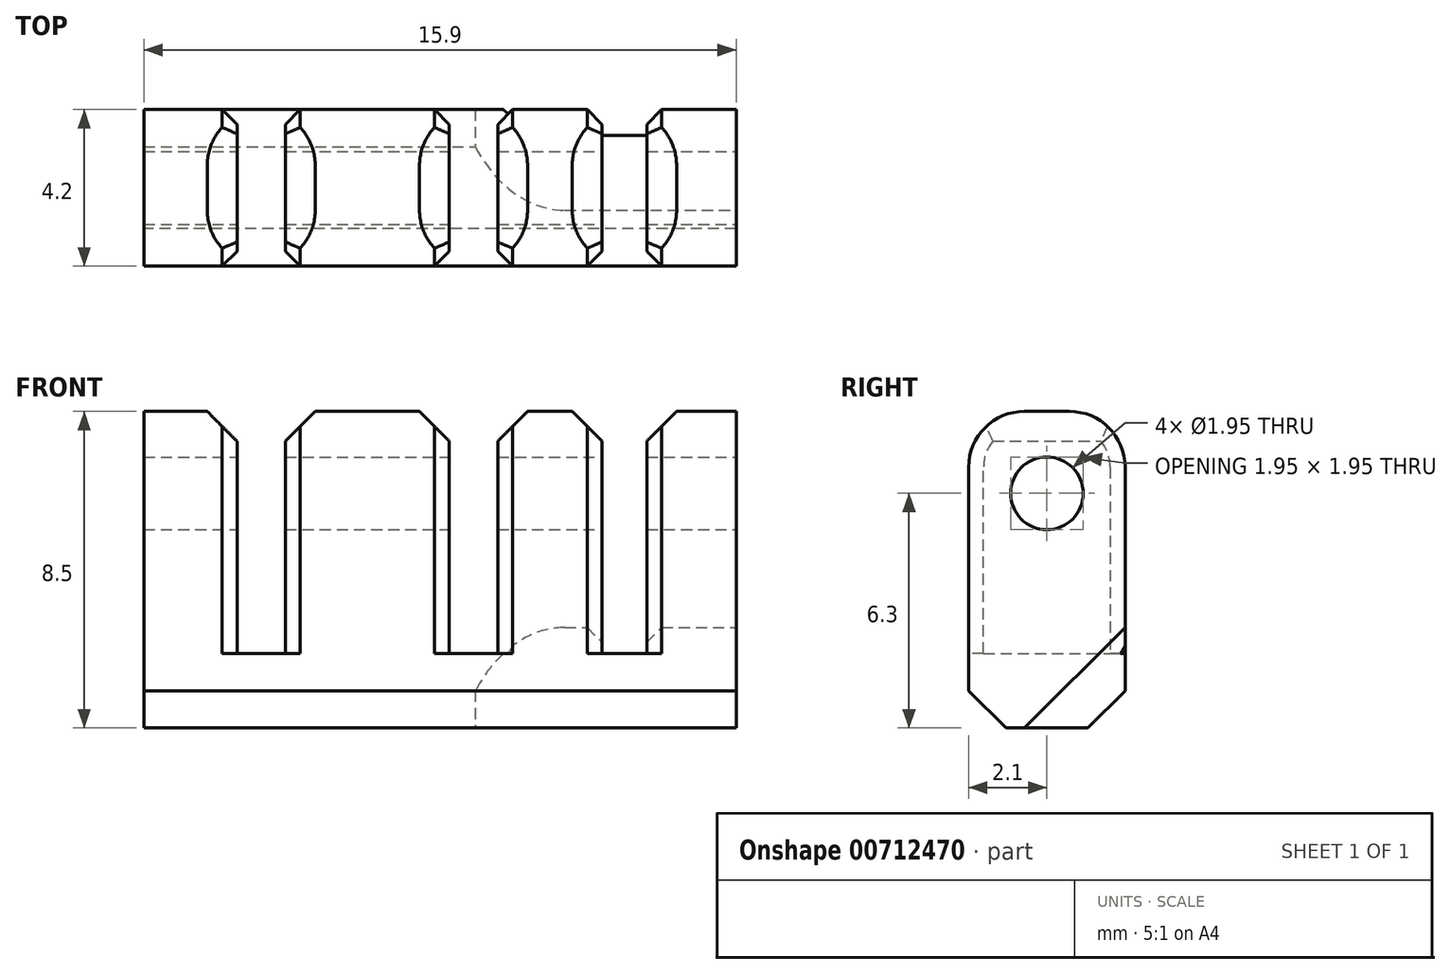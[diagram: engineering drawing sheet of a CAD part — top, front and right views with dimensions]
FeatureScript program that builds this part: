
annotation { "Feature Type Name" : "Feature", "Feature Type Description" : "" }
export const myFeature = defineFeature(function(context is Context, id is Id, definition is map)
    precondition{}
    {
        {
            var Q0;
            Q0=qCreatedBy(makeId("Front.planeOp"),FACE);
            var sketch = newSketch(context, id + "F0", { "sketchPlane" : qUnion([Q0])});
            skLineSegment(sketch, "E0", {"start": v(0, 0) * mm, "end": v(15.9, 0) * mm});
            skLineSegment(sketch, "E1", {"start": v(15.9, 0) * mm, "end": v(15.9, 8.5) * mm});
            skLineSegment(sketch, "E2", {"start": v(15.9, 8.5) * mm, "end": v(13.5, 8.5) * mm});
            skLineSegment(sketch, "E3", {"start": v(13.5, 8.5) * mm, "end": v(13.5, 2) * mm});
            skLineSegment(sketch, "E4", {"start": v(13.5, 2) * mm, "end": v(12.3, 2) * mm});
            skLineSegment(sketch, "E5", {"start": v(12.3, 2) * mm, "end": v(12.3, 8.5) * mm});
            skLineSegment(sketch, "E6", {"start": v(12.3, 8.5) * mm, "end": v(9.5, 8.5) * mm});
            skLineSegment(sketch, "E7", {"start": v(9.5, 8.5) * mm, "end": v(9.5, 2) * mm});
            skLineSegment(sketch, "E8", {"start": v(9.5, 2) * mm, "end": v(8.2, 2) * mm});
            skLineSegment(sketch, "E9", {"start": v(8.2, 2) * mm, "end": v(8.2, 8.5) * mm});
            skLineSegment(sketch, "E10", {"start": v(8.2, 8.5) * mm, "end": v(3.8, 8.5) * mm});
            skLineSegment(sketch, "E11", {"start": v(3.8, 8.5) * mm, "end": v(3.8, 2) * mm});
            skLineSegment(sketch, "E12", {"start": v(3.8, 2) * mm, "end": v(2.5, 2) * mm});
            skLineSegment(sketch, "E13", {"start": v(2.5, 2) * mm, "end": v(2.5, 8.5) * mm});
            skLineSegment(sketch, "E14", {"start": v(2.5, 8.5) * mm, "end": v(0, 8.5) * mm});
            skLineSegment(sketch, "E15", {"start": v(0, 8.5) * mm, "end": v(0, 0) * mm});
            skSolve(sketch);
        }
        {
            var Q0;
            Q0=makeQuery(id+"F0.imprint","IMPRINT",FACE,{"disambiguationData":[TD([[makeQuery(id+"F0.imprint","IMPRINT",EDGE,{"derivedFrom":sQuery(id+"F0.wireOp",EDGE,"E0")}),1.0]])]});
            extrude(context, id + "F1", {"entities" : qUnion([Q0]), "depth" : 4.2 * mm, "offsetDistance" : 25 * mm});
        }
        {
            var Q0;
            Q0=makeQuery(id+"F1.opExtrude","SWEPT_FACE",FACE,{"disambiguationData":[OSD([sQuery(id+"F0.wireOp",EDGE,"E1")])]});
            var sketch = newSketch(context, id + "F2", { "sketchPlane" : qUnion([Q0])});
            skCircle(sketch, "E16", {"center": v(-2.1, 6.3) * mm, "radius": 0.97 * mm});
            skSolve(sketch);
        }
        {
            var Q0;
            Q0=makeQuery(id+"F2.imprint","IMPRINT",FACE,{"disambiguationData":[TD([[makeQuery(id+"F2.imprint","IMPRINT",EDGE,{"derivedFrom":sQuery(id+"F2.wireOp",EDGE,"E16")}),1.0]])]});
            extrude(context, id + "F3", {"entities" : qUnion([Q0]), "operationType" : NewBodyOperationType.REMOVE, "oppositeDirection" : true, "depth" : 17.4 * mm, "offsetDistance" : 25 * mm});
        }
        {
            var Q0;
            Q0=makeQuery(id+"F1.opExtrude","SWEPT_EDGE",EDGE,{"disambiguationData":[OSD([sQuery(id+"F0.wireOp",EDGE,"E2"),sQuery(id+"F0.wireOp",EDGE,"E3")])]});
            var Q1;
            Q1=makeQuery(id+"F1.opExtrude","SWEPT_EDGE",EDGE,{"disambiguationData":[OSD([sQuery(id+"F0.wireOp",EDGE,"E5"),sQuery(id+"F0.wireOp",EDGE,"E6")])]});
            var Q2;
            Q2=makeQuery(id+"F1.opExtrude","SWEPT_EDGE",EDGE,{"disambiguationData":[OSD([sQuery(id+"F0.wireOp",EDGE,"E6"),sQuery(id+"F0.wireOp",EDGE,"E7")])]});
            var Q3;
            Q3=makeQuery(id+"F1.opExtrude","SWEPT_EDGE",EDGE,{"disambiguationData":[OSD([sQuery(id+"F0.wireOp",EDGE,"E9"),sQuery(id+"F0.wireOp",EDGE,"E10")])]});
            var Q4;
            Q4=makeQuery(id+"F1.opExtrude","SWEPT_EDGE",EDGE,{"disambiguationData":[OSD([sQuery(id+"F0.wireOp",EDGE,"E10"),sQuery(id+"F0.wireOp",EDGE,"E11")])]});
            var Q5;
            Q5=makeQuery(id+"F1.opExtrude","SWEPT_EDGE",EDGE,{"disambiguationData":[OSD([sQuery(id+"F0.wireOp",EDGE,"E13"),sQuery(id+"F0.wireOp",EDGE,"E14")])]});
            chamfer(context, id + "F4", {"entities" : qUnion([Q0, Q1, Q2, Q3, Q4, Q5]), "width" : 0.8 * mm, "tangentPropagation" : true});
        }
        {
            var Q0;
            Q0=makeQuery(id+"F1.opExtrude","CAP_EDGE",EDGE,{"disambiguationData":[OSD([sQuery(id+"F0.wireOp",EDGE,"E2")])],"isStart":false});
            var Q1;
            Q1=makeQuery(id+"F1.opExtrude","CAP_EDGE",EDGE,{"disambiguationData":[OSD([sQuery(id+"F0.wireOp",EDGE,"E6")])],"isStart":false});
            var Q2;
            Q2=makeQuery(id+"F1.opExtrude","CAP_EDGE",EDGE,{"disambiguationData":[OSD([sQuery(id+"F0.wireOp",EDGE,"E10")])],"isStart":false});
            var Q3;
            Q3=makeQuery(id+"F1.opExtrude","CAP_EDGE",EDGE,{"disambiguationData":[OSD([sQuery(id+"F0.wireOp",EDGE,"E14")])],"isStart":false});
            var Q4;
            Q4=makeQuery(id+"F1.opExtrude","CAP_EDGE",EDGE,{"disambiguationData":[OSD([sQuery(id+"F0.wireOp",EDGE,"E14")])],"isStart":true});
            var Q5;
            Q5=makeQuery(id+"F1.opExtrude","CAP_EDGE",EDGE,{"disambiguationData":[OSD([sQuery(id+"F0.wireOp",EDGE,"E10")])],"isStart":true});
            var Q6;
            Q6=makeQuery(id+"F1.opExtrude","CAP_EDGE",EDGE,{"disambiguationData":[OSD([sQuery(id+"F0.wireOp",EDGE,"E6")])],"isStart":true});
            var Q7;
            Q7=makeQuery(id+"F1.opExtrude","CAP_EDGE",EDGE,{"disambiguationData":[OSD([sQuery(id+"F0.wireOp",EDGE,"E2")])],"isStart":true});
            fillet(context, id + "F5", {"entities" : qUnion([Q0, Q1, Q2, Q3, Q4, Q5, Q6, Q7]), "radius" : 1.5 * mm, "tangentPropagation" : true, "allowEdgeOverflow" : false});
        }
        {
            var Q0;
            Q0=makeQuery(id+"F1.opExtrude","SWEPT_EDGE",EDGE,{"disambiguationData":[OSD([sQuery(id+"F0.wireOp",EDGE,"E13"),sQuery(id+"F0.wireOp",EDGE,"E14")])]});
            var Q1;
            Q1=makeQuery(id+"F5.opFillet","BLEND_EDGE",EDGE,{"blendedFrom":[makeQuery(id+"F1.opExtrude","CAP_EDGE",EDGE,{"disambiguationData":[OSD([sQuery(id+"F0.wireOp",EDGE,"E14")])],"isStart":false}),makeQuery(id+"F1.opExtrude","SWEPT_FACE",FACE,{"disambiguationData":[OSD([sQuery(id+"F0.wireOp",EDGE,"E13")])]})],"blendedInto":[makeQuery(id+"F1.opExtrude","SWEPT_FACE",FACE,{"disambiguationData":[OSD([sQuery(id+"F0.wireOp",EDGE,"E13")])]})]});
            var Q2;
            Q2=makeQuery(id+"F1.opExtrude","CAP_EDGE",EDGE,{"disambiguationData":[OSD([sQuery(id+"F0.wireOp",EDGE,"E13")])],"isStart":false});
            var Q3;
            Q3=makeQuery(id+"F1.opExtrude","CAP_EDGE",EDGE,{"disambiguationData":[OSD([sQuery(id+"F0.wireOp",EDGE,"E13")])],"isStart":true});
            var Q4;
            Q4=makeQuery(id+"F1.opExtrude","CAP_EDGE",EDGE,{"disambiguationData":[OSD([sQuery(id+"F0.wireOp",EDGE,"E11")])],"isStart":false});
            var Q5;
            Q5=makeQuery(id+"F1.opExtrude","CAP_EDGE",EDGE,{"disambiguationData":[OSD([sQuery(id+"F0.wireOp",EDGE,"E9")])],"isStart":false});
            var Q6;
            Q6=makeQuery(id+"F1.opExtrude","CAP_EDGE",EDGE,{"disambiguationData":[OSD([sQuery(id+"F0.wireOp",EDGE,"E7")])],"isStart":false});
            var Q7;
            Q7=makeQuery(id+"F1.opExtrude","CAP_EDGE",EDGE,{"disambiguationData":[OSD([sQuery(id+"F0.wireOp",EDGE,"E5")])],"isStart":false});
            var Q8;
            Q8=makeQuery(id+"F1.opExtrude","CAP_EDGE",EDGE,{"disambiguationData":[OSD([sQuery(id+"F0.wireOp",EDGE,"E3")])],"isStart":false});
            var Q9;
            Q9=makeQuery(id+"F1.opExtrude","CAP_EDGE",EDGE,{"disambiguationData":[OSD([sQuery(id+"F0.wireOp",EDGE,"E3")])],"isStart":true});
            var Q10;
            Q10=makeQuery(id+"F1.opExtrude","CAP_EDGE",EDGE,{"disambiguationData":[OSD([sQuery(id+"F0.wireOp",EDGE,"E5")])],"isStart":true});
            var Q11;
            Q11=makeQuery(id+"F1.opExtrude","CAP_EDGE",EDGE,{"disambiguationData":[OSD([sQuery(id+"F0.wireOp",EDGE,"E7")])],"isStart":true});
            var Q12;
            Q12=makeQuery(id+"F1.opExtrude","CAP_EDGE",EDGE,{"disambiguationData":[OSD([sQuery(id+"F0.wireOp",EDGE,"E9")])],"isStart":true});
            var Q13;
            Q13=makeQuery(id+"F1.opExtrude","CAP_EDGE",EDGE,{"disambiguationData":[OSD([sQuery(id+"F0.wireOp",EDGE,"E11")])],"isStart":true});
            chamfer(context, id + "F6", {"entities" : qUnion([Q0, Q1, Q2, Q3, Q4, Q5, Q6, Q7, Q8, Q9, Q10, Q11, Q12, Q13]), "width" : 0.4 * mm, "tangentPropagation" : true});
        }
        {
            var Q0;
            Q0=makeQuery(id+"F1.opExtrude","CAP_EDGE",EDGE,{"disambiguationData":[OSD([sQuery(id+"F0.wireOp",EDGE,"E0")])],"isStart":false});
            var Q1;
            Q1=makeQuery(id+"F1.opExtrude","CAP_EDGE",EDGE,{"disambiguationData":[OSD([sQuery(id+"F0.wireOp",EDGE,"E0")])],"isStart":true});
            chamfer(context, id + "F7", {"entities" : qUnion([Q0, Q1]), "width" : 1 * mm, "tangentPropagation" : true});
        }
        {
            var Q0;
            Q0=makeQuery(id+"F1.opExtrude","SWEPT_FACE",FACE,{"disambiguationData":[OSD([sQuery(id+"F0.wireOp",EDGE,"E1")])]});
            var sketch = newSketch(context, id + "F8", { "sketchPlane" : qUnion([Q0])});
            skLineSegment(sketch, "E17", {"start": v(-2.7, 0) * mm, "end": v(0, 2.7) * mm});
            skLineSegment(sketch, "E18", {"start": v(0, 2.7) * mm, "end": v(0, 0) * mm});
            skLineSegment(sketch, "E19", {"start": v(0, 0) * mm, "end": v(-2.7, 0) * mm});
            skSolve(sketch);
        }
        {
            var Q0;
            {var subQ0=sQuery(id+"F8.wireOp",EDGE,"E17");Q0=makeQuery(id+"F8.imprint","IMPRINT",FACE,{"disambiguationData":[TD([[makeQuery(id+"F8.imprint","IMPRINT",EDGE,{"derivedFrom":subQ0}),-1.0]])]});}
            extrude(context, id + "F9", {"entities" : qUnion([Q0]), "operationType" : NewBodyOperationType.REMOVE, "depth" : -7 * mm, "offsetDistance" : 25 * mm});
        }
        {
            var Q0;
            Q0=makeQuery(id+"F9.boolean.opBoolean","COPY",EDGE,{"derivedFrom":makeQuery(id+"F9.opExtrude","CAP_EDGE",EDGE,{"disambiguationData":[OSD([sQuery(id+"F8.wireOp",EDGE,"E17")])],"isStart":false})});
            fillet(context, id + "F10", {"entities" : qUnion([Q0]), "radius" : 3 * mm, "tangentPropagation" : true, "allowEdgeOverflow" : false});
        }
    });
